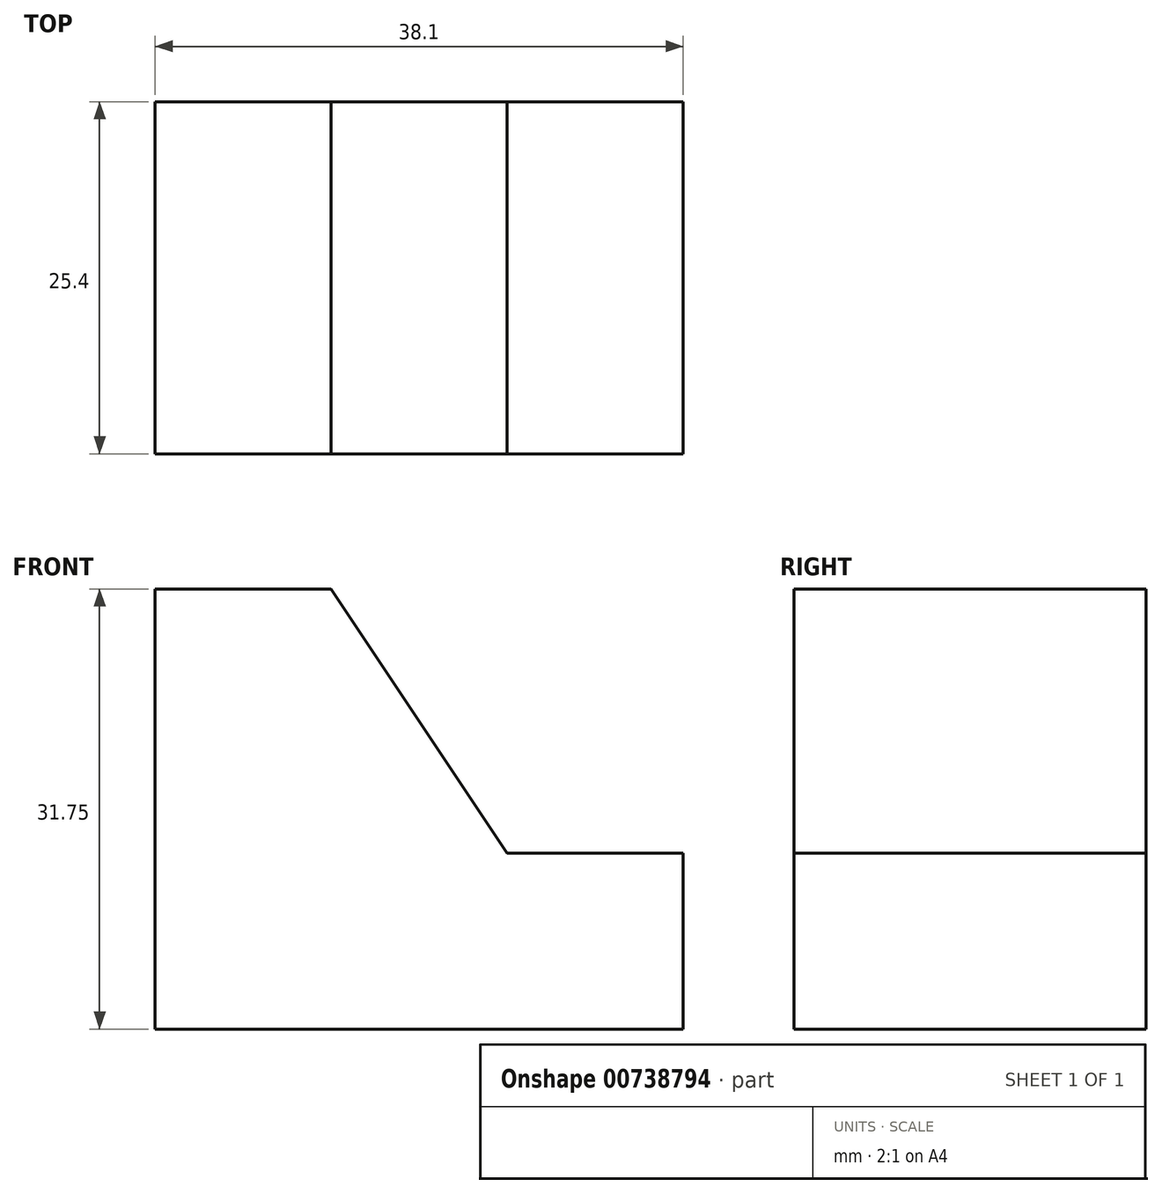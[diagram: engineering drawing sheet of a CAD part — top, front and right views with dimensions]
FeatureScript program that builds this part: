
annotation { "Feature Type Name" : "Feature", "Feature Type Description" : "" }
export const myFeature = defineFeature(function(context is Context, id is Id, definition is map)
    precondition{}
    {
        {
            var Q0;
            Q0=qCreatedBy(makeId("Front.planeOp"),FACE);
            var sketch = newSketch(context, id + "F0", { "sketchPlane" : qUnion([Q0])});
            skLineSegment(sketch, "E0", {"start": v(-47.8, 56.51) * mm, "end": v(-47.8, 24.76) * mm});
            skLineSegment(sketch, "E1", {"start": v(-47.8, 24.76) * mm, "end": v(-9.7, 24.76) * mm});
            skLineSegment(sketch, "E2", {"start": v(-9.7, 24.76) * mm, "end": v(-9.7, 37.46) * mm});
            skLineSegment(sketch, "E3", {"start": v(-9.7, 37.46) * mm, "end": v(-22.4, 37.46) * mm});
            skLineSegment(sketch, "E4", {"start": v(-22.4, 37.46) * mm, "end": v(-35.1, 56.51) * mm});
            skLineSegment(sketch, "E5", {"start": v(-35.1, 56.51) * mm, "end": v(-47.8, 56.51) * mm});
            skSolve(sketch);
        }
        {
            var Q0;
            Q0 = qSketchRegion(id + "F0", true);
            extrude(context, id + "F1", {"entities" : qUnion([Q0]), "depth" : 25.4 * mm, "offsetDistance" : 25.4 * mm});
        }
    });
